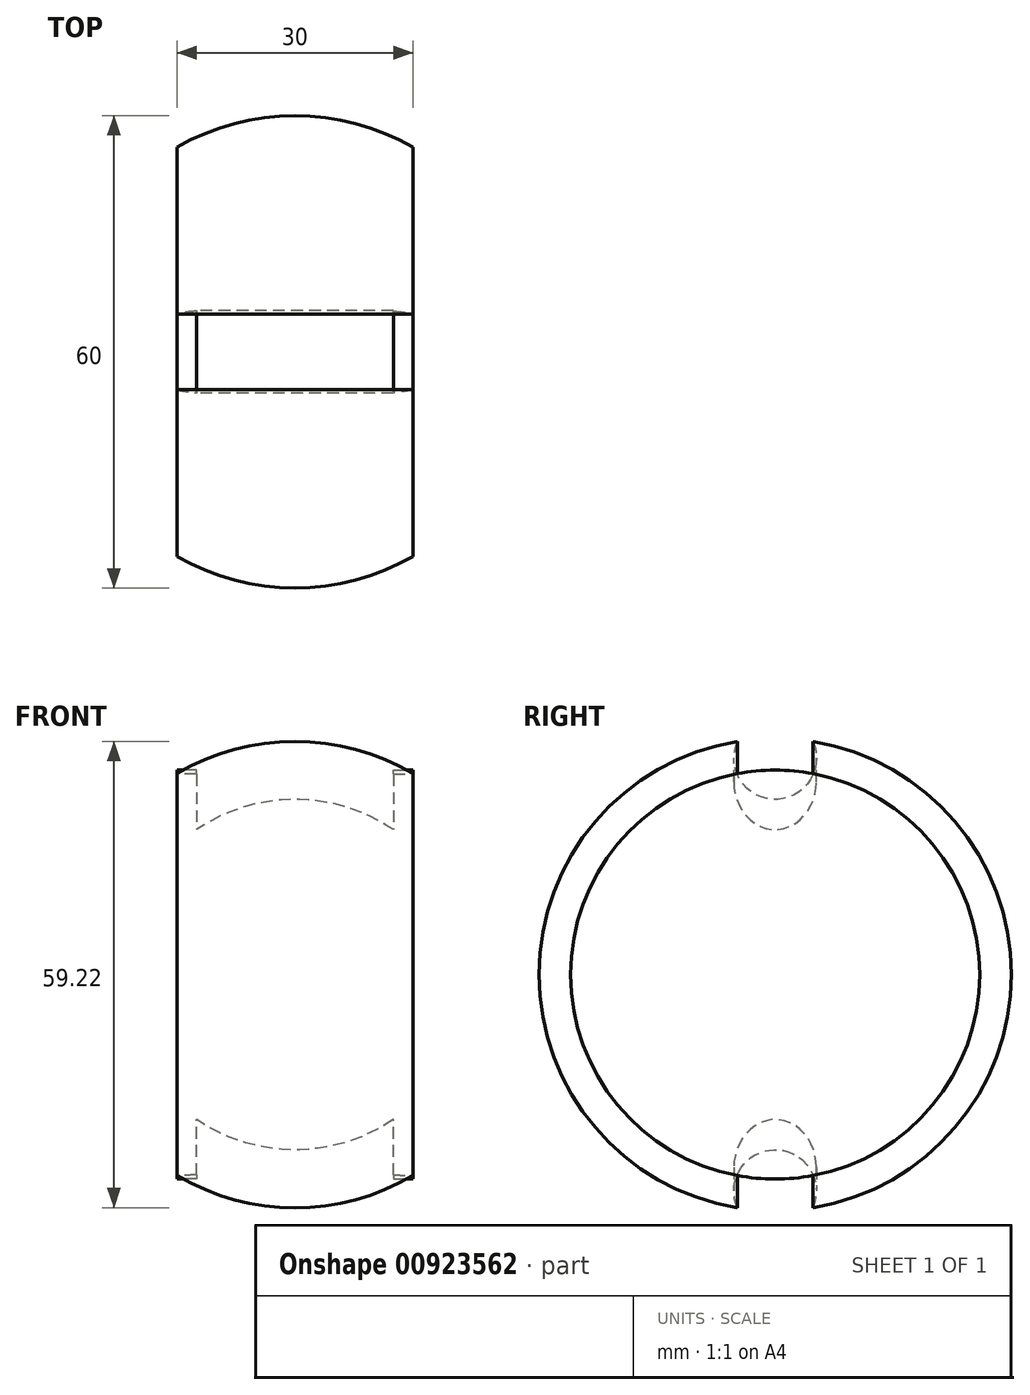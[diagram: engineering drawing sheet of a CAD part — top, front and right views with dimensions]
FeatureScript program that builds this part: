
annotation { "Feature Type Name" : "Feature", "Feature Type Description" : "" }
export const myFeature = defineFeature(function(context is Context, id is Id, definition is map)
    precondition{}
    {
        {
            var Q0;
            Q0=qCreatedBy(makeId("Front.planeOp"),FACE);
            var sketch = newSketch(context, id + "F0", { "sketchPlane" : qUnion([Q0])});
            skCircle(sketch, "E0", {"center": v(0, 0) * mm, "radius": 30 * mm, "construction": true});
            skLineSegment(sketch, "E1", {"start": v(-30, 0) * mm, "end": v(30, 0) * mm, "construction": true});
            skLineSegment(sketch, "E2", {"start": v(0, 30) * mm, "end": v(0, -30) * mm, "construction": true});
            skLineSegment(sketch, "E3", {"start": v(-15, 0) * mm, "end": v(-15, 25.98) * mm});
            skLineSegment(sketch, "E4", {"start": v(15, 0) * mm, "end": v(15, 25.98) * mm});
            skArc(sketch, "E5", {"start": v(15, 25.98) * mm, "mid": v(0, 30) * mm, "end": v(-15, 25.98) * mm});
            skLineSegment(sketch, "E6", {"start": v(-15, 0) * mm, "end": v(15, 0) * mm});
            skSolve(sketch);
        }
        {
            var Q0;
            Q0=makeQuery(id+"F0.imprint","IMPRINT",FACE,{"disambiguationData":[TD([[makeQuery(id+"F0.imprint","IMPRINT",EDGE,{"derivedFrom":sQuery(id+"F0.wireOp",EDGE,"E3")}),-1.0]])]});
            var Q1;
            Q1=sQuery(id+"F0.wireOp",EDGE,"E1");
            revolve(context, id + "F1", {"surfaceOperationType" : NewSurfaceOperationType.NEW, "entities" : qUnion([Q0]), "axis" : qUnion([Q1]), "revolveType" : RevolveType.FULL});
        }
        {
            var Q0;
            Q0=qCreatedBy(makeId("Right.planeOp"),FACE);
            var sketch = newSketch(context, id + "F2", { "sketchPlane" : qUnion([Q0])});
            skCircle(sketch, "E7", {"center": v(0, -27.5) * mm, "radius": 5.25 * mm});
            skLineSegment(sketch, "E8", {"start": v(0, 0) * mm, "end": v(30, 0) * mm, "construction": true});
            skSolve(sketch);
        }
        {
            var Q0;
            Q0=makeQuery(id+"F2.imprint","IMPRINT",FACE,{"disambiguationData":[TD([[makeQuery(id+"F2.imprint","IMPRINT",EDGE,{"derivedFrom":sQuery(id+"F2.wireOp",EDGE,"E7")}),1.0]])]});
            var Q1;
            Q1=sQuery(id+"F2.wireOp",EDGE,"E8");
            revolve(context, id + "F3", {"operationType" : NewBodyOperationType.REMOVE, "surfaceOperationType" : NewSurfaceOperationType.NEW, "entities" : qUnion([Q0]), "axis" : qUnion([Q1]), "revolveType" : RevolveType.FULL});
        }
        {
            var Q0;
            Q0=makeQuery(id+"F1.opRevolve","SWEPT_FACE",FACE,{"disambiguationData":[OSD([sQuery(id+"F0.wireOp",EDGE,"E3")])]});
            var sketch = newSketch(context, id + "F4", { "sketchPlane" : qUnion([Q0])});
            skCircle(sketch, "E9", {"center": v(0, 0) * mm, "radius": 25.98 * mm});
            skSolve(sketch);
        }
        {
            var Q0;
            Q0 = qSketchRegion(id + "F4", true);
            extrude(context, id + "F5", {"entities" : qUnion([Q0]), "operationType" : NewBodyOperationType.ADD, "oppositeDirection" : true, "depth" : 2.5 * mm, "offsetDistance" : 25 * mm});
        }
        {
            var Q0;
            Q0=makeQuery(id+"F1.opRevolve","SWEPT_BODY",BODY,{"disambiguationData":[OSD([sQuery(id+"F0.wireOp",EDGE,"E3"),sQuery(id+"F0.wireOp",EDGE,"E4"),sQuery(id+"F0.wireOp",EDGE,"E5"),sQuery(id+"F0.wireOp",EDGE,"E6")])]});
            var Q1;
            Q1=qCreatedBy(makeId("Right.planeOp"),FACE);
            mirror(context, id + "F6", {"operationType" : NewBodyOperationType.ADD, "entities" : qUnion([Q0]), "mirrorPlane" : qUnion([Q1])});
        }
    });
